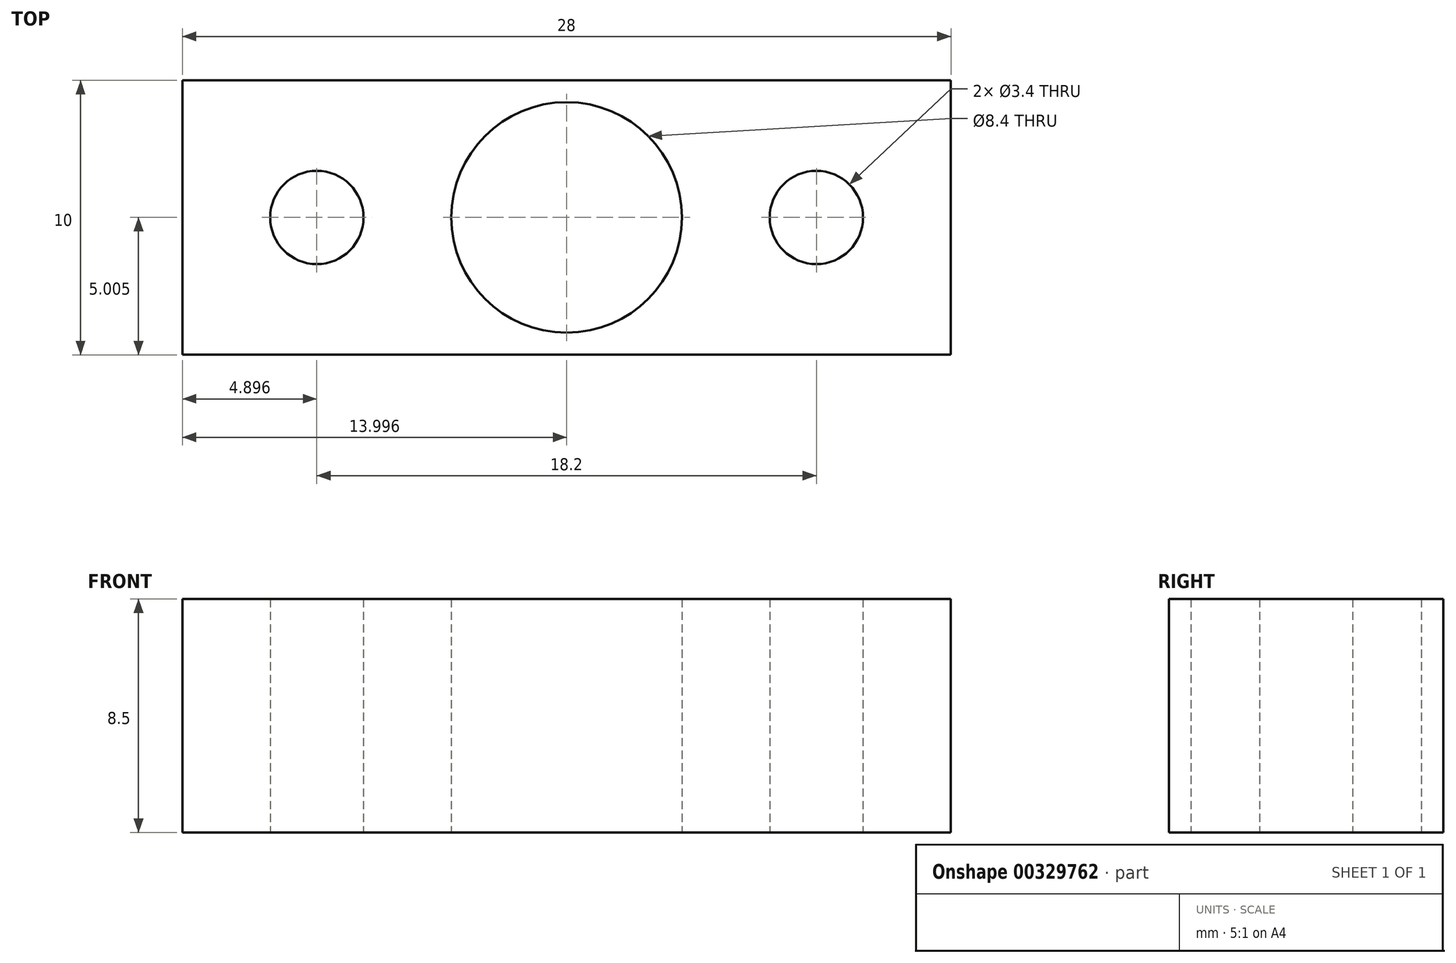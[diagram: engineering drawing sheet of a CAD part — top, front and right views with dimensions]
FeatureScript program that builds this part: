
annotation { "Feature Type Name" : "Feature", "Feature Type Description" : "" }
export const myFeature = defineFeature(function(context is Context, id is Id, definition is map)
    precondition{}
    {
        {
            var Q0;
            Q0=qCreatedBy(makeId("Top.planeOp"),FACE);
            var sketch = newSketch(context, id + "F0", { "sketchPlane" : qUnion([Q0])});
            skCircle(sketch, "E0", {"center": v(-41.95, 22.9) * mm, "radius": 4.2 * mm});
            skLineSegment(sketch, "E1", {"start": v(-41.95, 22.9) * mm, "end": v(-46.15, 22.9) * mm});
            skLineSegment(sketch, "E2", {"start": v(-46.15, 22.9) * mm, "end": v(-48.15, 22.9) * mm});
            skLineSegment(sketch, "E3", {"start": v(-48.15, 22.9) * mm, "end": v(-53.95, 22.9) * mm});
            skLineSegment(sketch, "E4", {"start": v(-53.95, 22.9) * mm, "end": v(-55.95, 22.9) * mm});
            skLineSegment(sketch, "E5", {"start": v(-55.95, 22.9) * mm, "end": v(-55.95, 27.9) * mm});
            skLineSegment(sketch, "E6", {"start": v(-55.95, 27.9) * mm, "end": v(-41.95, 27.9) * mm});
            skLineSegment(sketch, "E7", {"start": v(-41.95, 27.9) * mm, "end": v(-41.95, 22.9) * mm});
            skCircle(sketch, "E8.cCircle", {"center": v(-51.05, 22.9) * mm, "radius": 2.9 * mm, "construction": true});
            skLineSegment(sketch, "E8.0", {"start": v(-48.15, 24.58) * mm, "end": v(-48.15, 21.23) * mm});
            skLineSegment(sketch, "E8.1", {"start": v(-48.15, 21.23) * mm, "end": v(-51.05, 19.56) * mm});
            skLineSegment(sketch, "E8.2", {"start": v(-51.05, 19.56) * mm, "end": v(-53.95, 21.23) * mm});
            skLineSegment(sketch, "E8.3", {"start": v(-53.95, 21.23) * mm, "end": v(-53.95, 24.58) * mm});
            skLineSegment(sketch, "E8.4", {"start": v(-53.95, 24.58) * mm, "end": v(-51.05, 26.25) * mm});
            skLineSegment(sketch, "E8.5", {"start": v(-51.05, 26.25) * mm, "end": v(-48.15, 24.58) * mm});
            skPoint(sketch, "E8.0.midPoint", {"position": v(-48.15, 22.9) * mm});
            skCircle(sketch, "E9", {"center": v(-51.05, 22.9) * mm, "radius": 1.7 * mm});
            skLineSegment(sketch, "E10.MirrorCS", {"start": v(-55.95, 22.9) * mm, "end": v(-55.95, 17.9) * mm});
            skLineSegment(sketch, "E11.MirrorCS", {"start": v(-55.95, 17.9) * mm, "end": v(-41.95, 17.9) * mm});
            skLineSegment(sketch, "E12.MirrorCS", {"start": v(-41.95, 17.9) * mm, "end": v(-41.95, 22.9) * mm});
            skLineSegment(sketch, "E13.MirrorCS", {"start": v(-41.95, 22.9) * mm, "end": v(-37.75, 22.9) * mm});
            skLineSegment(sketch, "E14.MirrorCS", {"start": v(-35.75, 24.58) * mm, "end": v(-35.75, 21.23) * mm});
            skLineSegment(sketch, "E15.MirrorCS", {"start": v(-32.85, 26.25) * mm, "end": v(-35.75, 24.58) * mm});
            skLineSegment(sketch, "E16.MirrorCS", {"start": v(-29.95, 24.58) * mm, "end": v(-32.85, 26.25) * mm});
            skLineSegment(sketch, "E17.MirrorCS", {"start": v(-29.95, 21.23) * mm, "end": v(-29.95, 24.58) * mm});
            skLineSegment(sketch, "E18.MirrorCS", {"start": v(-32.85, 19.56) * mm, "end": v(-29.95, 21.23) * mm});
            skLineSegment(sketch, "E19.MirrorCS", {"start": v(-35.75, 21.23) * mm, "end": v(-32.85, 19.56) * mm});
            skLineSegment(sketch, "E20.MirrorCS", {"start": v(-27.95, 17.9) * mm, "end": v(-41.95, 17.9) * mm});
            skLineSegment(sketch, "E21.MirrorCS", {"start": v(-27.95, 22.9) * mm, "end": v(-27.95, 17.9) * mm});
            skLineSegment(sketch, "E22.MirrorCS", {"start": v(-27.95, 22.9) * mm, "end": v(-27.95, 27.9) * mm});
            skCircle(sketch, "E23.MirrorC", {"center": v(-32.85, 22.9) * mm, "radius": 1.7 * mm});
            skLineSegment(sketch, "E24.MirrorCS", {"start": v(-27.95, 27.9) * mm, "end": v(-41.95, 27.9) * mm});
            skSolve(sketch);
        }
        {
            var Q0;
            {var subQ3=sQuery(id+"F0.wireOp",EDGE,"E2");Q0=makeQuery(id+"F0.imprint","IMPRINT",FACE,{"disambiguationData":[TD([[makeQuery(id+"F0.imprint","IMPRINT",EDGE,{"derivedFrom":subQ3}),1.0]])]});}
            var Q1;
            {var subQ3=sQuery(id+"F0.wireOp",EDGE,"E8.1");Q1=makeQuery(id+"F0.imprint","IMPRINT",FACE,{"disambiguationData":[TD([[makeQuery(id+"F0.imprint","IMPRINT",EDGE,{"derivedFrom":subQ3}),-1.0]])]});}
            var Q2;
            {var subQ3=sQuery(id+"F0.wireOp",EDGE,"E8.4");Q2=makeQuery(id+"F0.imprint","IMPRINT",FACE,{"disambiguationData":[TD([[makeQuery(id+"F0.imprint","IMPRINT",EDGE,{"derivedFrom":subQ3}),-1.0]])]});}
            var Q3;
            {var subQ3=sQuery(id+"F0.wireOp",EDGE,"E2");Q3=makeQuery(id+"F0.imprint","IMPRINT",FACE,{"disambiguationData":[TD([[makeQuery(id+"F0.imprint","IMPRINT",EDGE,{"derivedFrom":subQ3}),-1.0]])]});}
            var Q4;
            Q4=makeQuery(id+"F0.imprint","IMPRINT",FACE,{"disambiguationData":[TD([[makeQuery(id+"F0.imprint","IMPRINT",EDGE,{"derivedFrom":sQuery(id+"F0.wireOp",EDGE,"E14.MirrorCS")}),-1.0]])]});
            var Q5;
            Q5=makeQuery(id+"F0.imprint","IMPRINT",FACE,{"disambiguationData":[TD([[makeQuery(id+"F0.imprint","IMPRINT",EDGE,{"derivedFrom":sQuery(id+"F0.wireOp",EDGE,"E14.MirrorCS")}),1.0]])]});
            extrude(context, id + "F1", {"entities" : qUnion([Q0, Q1, Q2, Q3, Q4, Q5]), "depth" : 8.5 * mm});
        }
    });
